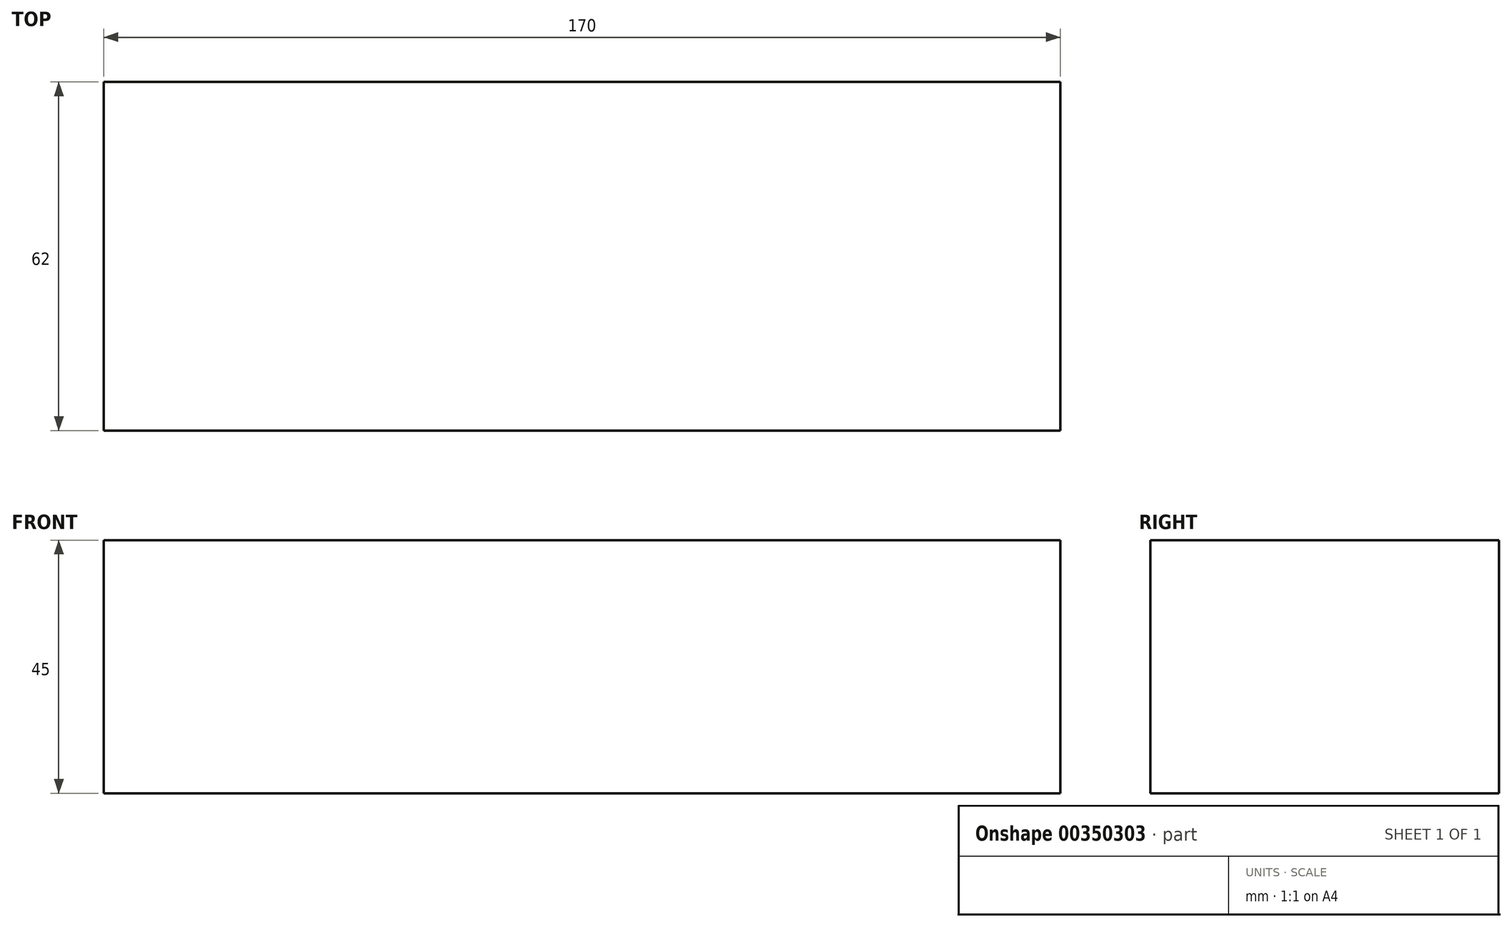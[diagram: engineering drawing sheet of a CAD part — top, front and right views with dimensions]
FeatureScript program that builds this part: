
annotation { "Feature Type Name" : "Feature", "Feature Type Description" : "" }
export const myFeature = defineFeature(function(context is Context, id is Id, definition is map)
    precondition{}
    {
        {
            var Q0;
            Q0=qCreatedBy(makeId("Top.planeOp"),FACE);
            var sketch = newSketch(context, id + "F0", { "sketchPlane" : qUnion([Q0])});
            skLineSegment(sketch, "E0.bottom", {"start": v(0, 0) * mm, "end": v(170, 0) * mm});
            skLineSegment(sketch, "E0.top", {"start": v(0, 62) * mm, "end": v(170, 62) * mm});
            skLineSegment(sketch, "E0.left", {"start": v(0, 0) * mm, "end": v(0, 62) * mm});
            skLineSegment(sketch, "E0.right", {"start": v(170, 0) * mm, "end": v(170, 62) * mm});
            skSolve(sketch);
        }
        {
            var Q0;
            Q0 = qSketchRegion(id + "F0", true);
            extrude(context, id + "F1", {"entities" : qUnion([Q0]), "depth" : 45 * mm});
        }
    });
